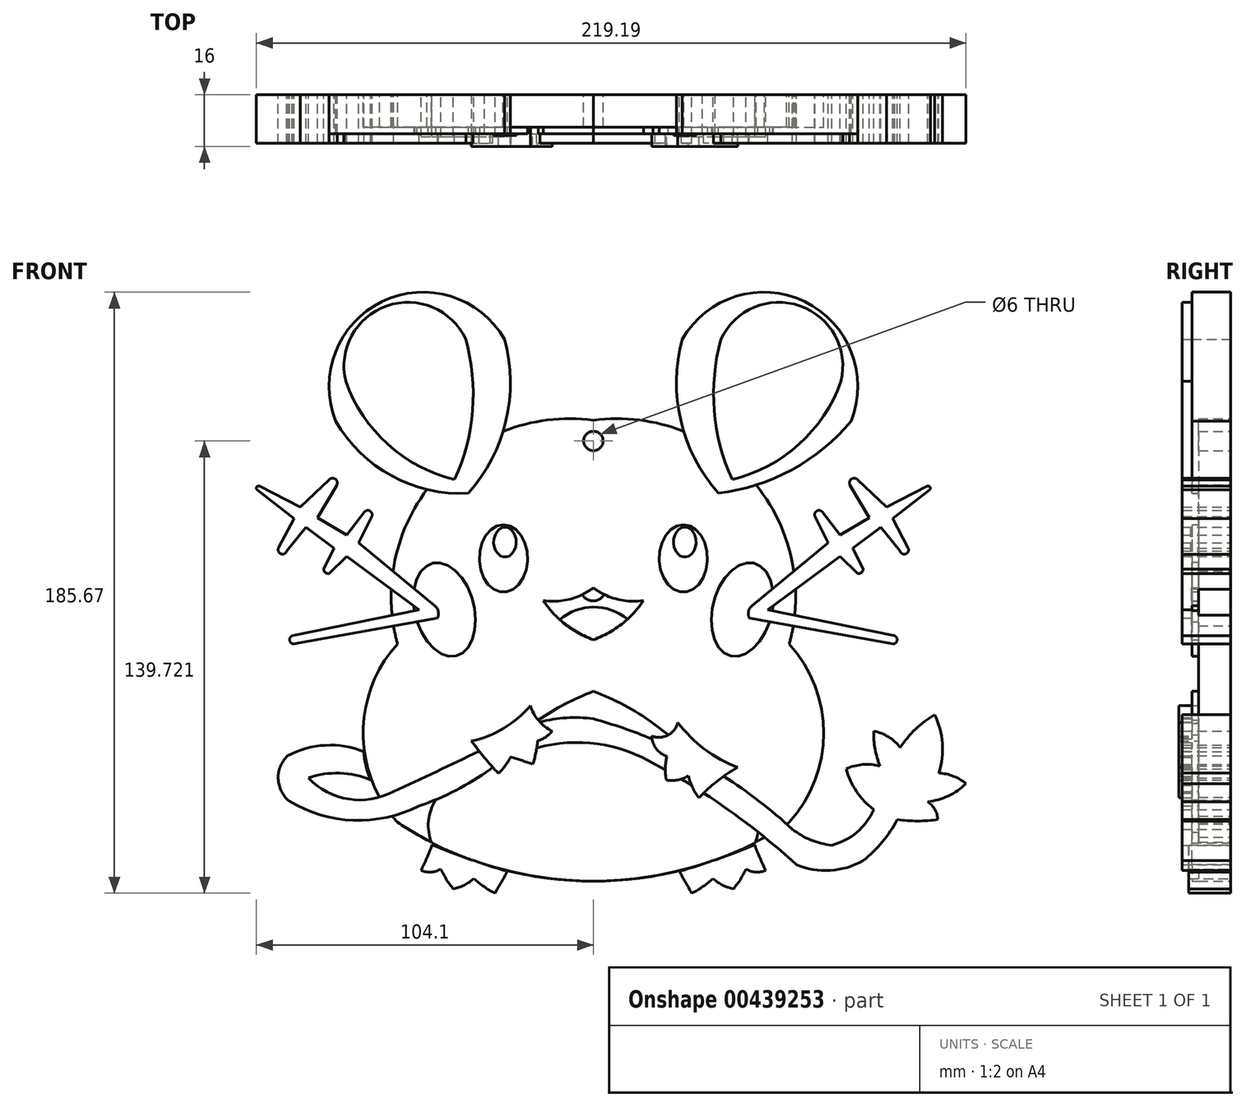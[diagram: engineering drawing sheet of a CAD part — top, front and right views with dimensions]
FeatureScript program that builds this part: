
annotation { "Feature Type Name" : "Feature", "Feature Type Description" : "" }
export const myFeature = defineFeature(function(context is Context, id is Id, definition is map)
    precondition{}
    {
        {
            var Q0;
            Q0=qCreatedBy(makeId("Front.planeOp"),FACE);
            var sketch = newSketch(context, id + "F0", { "sketchPlane" : qUnion([Q0])});
            skPoint(sketch, "E0", {"position": v(-60.51, 0) * mm});
            skPoint(sketch, "E1", {"position": v(0, 69.06) * mm});
            skArc(sketch, "E2", {"start": v(0, 69.06) * mm, "mid": v(-48.84, 50.82) * mm, "end": v(-60.51, 0) * mm});
            skLineSegment(sketch, "E3", {"start": v(0, 69.06) * mm, "end": v(0, -72.21) * mm, "construction": true});
            skArc(sketch, "E4.MirrorCS", {"start": v(0, 69.06) * mm, "mid": v(48.84, 50.82) * mm, "end": v(60.51, 0) * mm});
            skPoint(sketch, "E5", {"position": v(-60.51, -55.13) * mm});
            skArc(sketch, "E6", {"start": v(-60.51, 0) * mm, "mid": v(-71.12, -27.56) * mm, "end": v(-60.51, -55.13) * mm});
            skArc(sketch, "E7.MirrorCS", {"start": v(60.51, 0) * mm, "mid": v(71.12, -27.56) * mm, "end": v(60.51, -55.13) * mm});
            skArc(sketch, "E8", {"start": v(-60.51, -55.13) * mm, "mid": v(0, -73.32) * mm, "end": v(60.51, -55.13) * mm});
            skSolve(sketch);
        }
        {
            var Q0;
            Q0=qCreatedBy(makeId("Front.planeOp"),FACE);
            var sketch = newSketch(context, id + "F1", { "sketchPlane" : qUnion([Q0])});
            skEllipse(sketch, "E9", {"center": v(-27.78, 26.42) * mm, "majorRadius": 10.45 * mm, "minorRadius": 7.45 * mm, "majorAxis": v(0, 1)});
            skEllipse(sketch, "E10", {"center": v(-46, 10.64) * mm, "majorRadius": 14.77 * mm, "minorRadius": 9.16 * mm, "majorAxis": v(-0.25, 0.97)});
            skEllipse(sketch, "E11.MirrorC", {"center": v(46, 10.64) * mm, "majorRadius": 14.77 * mm, "minorRadius": 9.16 * mm, "majorAxis": v(0.25, 0.97)});
            skEllipse(sketch, "E12.MirrorC", {"center": v(27.78, 26.42) * mm, "majorRadius": 10.45 * mm, "minorRadius": 7.45 * mm, "majorAxis": v(0, 1)});
            skEllipse(sketch, "E13", {"center": v(-27.3, 31.45) * mm, "majorRadius": 4.6 * mm, "minorRadius": 3.5 * mm, "majorAxis": v(0, 1)});
            skPoint(sketch, "E14.endSnap0", {"position": v(-30.8, 31.45) * mm});
            skPoint(sketch, "E15", {"position": v(-34.3, 31.45) * mm});
            skPoint(sketch, "E16", {"position": v(21.25, 31.45) * mm});
            skPoint(sketch, "E17", {"position": v(28.25, 31.45) * mm});
            skPoint(sketch, "E18", {"position": v(-27.3, 36.05) * mm});
            skLineSegment(sketch, "E19", {"start": v(28.25, 36.05) * mm, "end": v(28.25, 40.65) * mm});
            skPoint(sketch, "E20", {"position": v(28.25, 36.05) * mm});
            skEllipse(sketch, "E21", {"center": v(28.25, 31.45) * mm, "majorRadius": 4.6 * mm, "minorRadius": 3.5 * mm, "majorAxis": v(0, 1)});
            skPoint(sketch, "E22", {"position": v(-23.8, 31.45) * mm});
            skPoint(sketch, "E23", {"position": v(24.75, 31.45) * mm});
            skPoint(sketch, "E24", {"position": v(31.75, 31.45) * mm});
            skPoint(sketch, "E14.end.orphan", {"position": v(-36.36, 31.45) * mm});
            skPoint(sketch, "E25", {"position": v(0, 17.34) * mm});
            skPoint(sketch, "E26", {"position": v(-18.45, 14.06) * mm});
            skArc(sketch, "E27", {"start": v(-18.45, 14.06) * mm, "mid": v(-8.83, 13.48) * mm, "end": v(0, 17.34) * mm});
            skArc(sketch, "E28.MirrorCS", {"start": v(18.45, 14.06) * mm, "mid": v(8.83, 13.48) * mm, "end": v(0, 17.34) * mm});
            skPoint(sketch, "E29", {"position": v(0, 0) * mm});
            skPoint(sketch, "E30", {"position": v(0, 1.29) * mm});
            skPoint(sketch, "E31", {"position": v(0, 10.13) * mm});
            skPoint(sketch, "E32", {"position": v(-5.69, 14.3) * mm});
            skArc(sketch, "E33", {"start": v(-5.69, 14.3) * mm, "mid": v(-3.15, 11.8) * mm, "end": v(0, 10.13) * mm});
            skArc(sketch, "E34.MirrorCS", {"start": v(5.69, 14.3) * mm, "mid": v(3.15, 11.8) * mm, "end": v(0, 10.13) * mm});
            skArc(sketch, "E35", {"start": v(-15.44, 13.38) * mm, "mid": v(-8.7, 6.08) * mm, "end": v(0, 1.29) * mm});
            skArc(sketch, "E36.MirrorCS", {"start": v(15.44, 13.38) * mm, "mid": v(8.7, 6.08) * mm, "end": v(0, 1.29) * mm});
            skPoint(sketch, "E37", {"position": v(-79.58, 68.87) * mm});
            skPoint(sketch, "E38", {"position": v(-38.6, 46.57) * mm});
            skPoint(sketch, "E39", {"position": v(-27.45, 94.11) * mm});
            skArc(sketch, "E40", {"start": v(-79.58, 68.87) * mm, "mid": v(-62.27, 51.88) * mm, "end": v(-38.6, 46.57) * mm});
            skArc(sketch, "E41", {"start": v(-38.6, 46.57) * mm, "mid": v(-27, 68.93) * mm, "end": v(-27.45, 94.11) * mm});
            skArc(sketch, "E42", {"start": v(-27.45, 94.11) * mm, "mid": v(-65.26, 105.75) * mm, "end": v(-79.58, 68.87) * mm});
            skArc(sketch, "E43.MirrorCS", {"start": v(38.6, 46.57) * mm, "mid": v(27, 68.93) * mm, "end": v(27.45, 94.11) * mm});
            skArc(sketch, "E44.MirrorCS", {"start": v(27.45, 94.11) * mm, "mid": v(65.26, 105.75) * mm, "end": v(79.58, 68.87) * mm});
            skArc(sketch, "E45", {"start": v(38.6, 46.57) * mm, "mid": v(61.26, 53.74) * mm, "end": v(79.58, 68.87) * mm});
            skPoint(sketch, "E46", {"position": v(0, -14.65) * mm});
            skPoint(sketch, "E47", {"position": v(-18.44, -24.49) * mm});
            skPoint(sketch, "E48", {"position": v(-49.92, -61.53) * mm});
            skPoint(sketch, "E49", {"position": v(-48.16, -47.4) * mm});
            skArc(sketch, "E50", {"start": v(0, -14.65) * mm, "mid": v(-9.54, -18.97) * mm, "end": v(-18.44, -24.49) * mm});
            skArc(sketch, "E51", {"start": v(-48.16, -47.4) * mm, "mid": v(-50.9, -54.23) * mm, "end": v(-49.92, -61.53) * mm});
            skLineSegment(sketch, "E52", {"start": v(-18.44, -24.49) * mm, "end": v(-48.16, -47.4) * mm});
            skArc(sketch, "E53.MirrorCS", {"start": v(0, -14.65) * mm, "mid": v(9.54, -18.97) * mm, "end": v(18.44, -24.49) * mm});
            skLineSegment(sketch, "E54.MirrorCS", {"start": v(18.44, -24.49) * mm, "end": v(48.16, -47.4) * mm});
            skArc(sketch, "E55.MirrorCS", {"start": v(48.16, -47.4) * mm, "mid": v(50.9, -54.23) * mm, "end": v(49.92, -61.53) * mm});
            skArc(sketch, "E56", {"start": v(-49.92, -61.53) * mm, "mid": v(0, -73.23) * mm, "end": v(49.92, -61.53) * mm});
            skSolve(sketch);
        }
        {
            var Q0;
            Q0=qCreatedBy(makeId("Front.planeOp"),FACE);
            var sketch = newSketch(context, id + "F2", { "sketchPlane" : qUnion([Q0])});
            skLineSegment(sketch, "E57", {"start": v(-48.16, 7.98) * mm, "end": v(-92.67, 0) * mm});
            skPoint(sketch, "E58", {"position": v(-93.06, 2.5) * mm});
            skPoint(sketch, "E59", {"position": v(-48.96, 11.76) * mm});
            skArc(sketch, "E60", {"start": v(-93.06, 2.5) * mm, "mid": v(-93.82, 1.1) * mm, "end": v(-92.67, 0) * mm});
            skArc(sketch, "E61", {"start": v(-48.16, 7.98) * mm, "mid": v(-47.9, 10.01) * mm, "end": v(-48.96, 11.76) * mm});
            skLineSegment(sketch, "E62", {"start": v(-93.06, 2.5) * mm, "end": v(-53.87, 10.6) * mm});
            skLineSegment(sketch, "E63", {"start": v(-53.87, 10.6) * mm, "end": v(-76.2, 27) * mm});
            skLineSegment(sketch, "E64", {"start": v(-76.2, 27) * mm, "end": v(-81.72, 21.76) * mm});
            skLineSegment(sketch, "E65", {"start": v(-48.96, 11.76) * mm, "end": v(-72.48, 31.21) * mm});
            skLineSegment(sketch, "E66", {"start": v(-72.48, 31.21) * mm, "end": v(-68.43, 39.4) * mm});
            skPoint(sketch, "E67", {"position": v(-83.3, 23.07) * mm});
            skPoint(sketch, "E68", {"position": v(-70.75, 40.72) * mm});
            skPoint(sketch, "E69", {"position": v(-79.3, 48.99) * mm});
            skPoint(sketch, "E70", {"position": v(-81.72, 50.64) * mm});
            skPoint(sketch, "E71", {"position": v(-103.83, 47.6) * mm});
            skPoint(sketch, "E72", {"position": v(-103.15, 48.71) * mm});
            skPoint(sketch, "E73", {"position": v(-97.22, 29.69) * mm});
            skPoint(sketch, "E74", {"position": v(-94.74, 28.72) * mm});
            skLineSegment(sketch, "E75", {"start": v(-80.13, 29.55) * mm, "end": v(-87.57, 35.2) * mm});
            skLineSegment(sketch, "E76", {"start": v(-79.3, 48.99) * mm, "end": v(-85.23, 38.92) * mm});
            skLineSegment(sketch, "E77", {"start": v(-85.23, 38.92) * mm, "end": v(-76.2, 33.6) * mm});
            skLineSegment(sketch, "E78", {"start": v(-76.2, 33.6) * mm, "end": v(-70.75, 40.72) * mm});
            skLineSegment(sketch, "E79", {"start": v(-97.22, 29.69) * mm, "end": v(-92.4, 38.79) * mm});
            skLineSegment(sketch, "E80", {"start": v(-92.4, 38.79) * mm, "end": v(-103.83, 47.6) * mm});
            skLineSegment(sketch, "E81", {"start": v(-103.15, 48.71) * mm, "end": v(-90.6, 42.23) * mm});
            skLineSegment(sketch, "E82", {"start": v(-90.6, 42.23) * mm, "end": v(-81.72, 50.64) * mm});
            skArc(sketch, "E83", {"start": v(-103.15, 48.71) * mm, "mid": v(-104, 48.48) * mm, "end": v(-103.83, 47.6) * mm});
            skArc(sketch, "E84", {"start": v(-97.22, 29.69) * mm, "mid": v(-96.52, 27.81) * mm, "end": v(-94.74, 28.72) * mm});
            skLineSegment(sketch, "E85", {"start": v(-94.74, 28.72) * mm, "end": v(-88.74, 36.09) * mm});
            skLineSegment(sketch, "E86", {"start": v(-88.74, 36.09) * mm, "end": v(-87.57, 35.2) * mm});
            skArc(sketch, "E87", {"start": v(-79.3, 48.99) * mm, "mid": v(-79.73, 50.94) * mm, "end": v(-81.72, 50.64) * mm});
            skArc(sketch, "E88", {"start": v(-68.43, 39.4) * mm, "mid": v(-69.02, 41.07) * mm, "end": v(-70.75, 40.72) * mm});
            skArc(sketch, "E89", {"start": v(-83.3, 23.07) * mm, "mid": v(-82.8, 22.05) * mm, "end": v(-81.72, 21.76) * mm});
            skLineSegment(sketch, "E90", {"start": v(-80.13, 29.55) * mm, "end": v(-83.3, 23.07) * mm});
            skLineSegment(sketch, "E91.MirrorCS", {"start": v(103.15, 48.71) * mm, "end": v(90.6, 42.23) * mm});
            skArc(sketch, "E92.MirrorCS", {"start": v(103.15, 48.71) * mm, "mid": v(104, 48.48) * mm, "end": v(103.83, 47.6) * mm});
            skLineSegment(sketch, "E93.MirrorCS", {"start": v(92.4, 38.79) * mm, "end": v(103.83, 47.6) * mm});
            skLineSegment(sketch, "E94.MirrorCS", {"start": v(90.6, 42.23) * mm, "end": v(81.72, 50.64) * mm});
            skArc(sketch, "E95.MirrorCS", {"start": v(79.3, 48.99) * mm, "mid": v(79.73, 50.94) * mm, "end": v(81.72, 50.64) * mm});
            skLineSegment(sketch, "E96.MirrorCS", {"start": v(79.3, 48.99) * mm, "end": v(85.23, 38.92) * mm});
            skLineSegment(sketch, "E97.MirrorCS", {"start": v(97.22, 29.69) * mm, "end": v(92.4, 38.79) * mm});
            skArc(sketch, "E98.MirrorCS", {"start": v(97.22, 29.69) * mm, "mid": v(96.52, 27.81) * mm, "end": v(94.74, 28.72) * mm});
            skLineSegment(sketch, "E99.MirrorCS", {"start": v(94.74, 28.72) * mm, "end": v(88.74, 36.09) * mm});
            skLineSegment(sketch, "E100.MirrorCS", {"start": v(80.13, 29.55) * mm, "end": v(87.57, 35.2) * mm});
            skLineSegment(sketch, "E101.MirrorCS", {"start": v(88.74, 36.09) * mm, "end": v(87.57, 35.2) * mm});
            skLineSegment(sketch, "E102.MirrorCS", {"start": v(80.13, 29.55) * mm, "end": v(83.3, 23.07) * mm});
            skArc(sketch, "E103.MirrorCS", {"start": v(83.3, 23.07) * mm, "mid": v(82.8, 22.05) * mm, "end": v(81.72, 21.76) * mm});
            skLineSegment(sketch, "E104.MirrorCS", {"start": v(76.2, 27) * mm, "end": v(81.72, 21.76) * mm});
            skLineSegment(sketch, "E105.MirrorCS", {"start": v(53.87, 10.6) * mm, "end": v(76.2, 27) * mm});
            skLineSegment(sketch, "E106.MirrorCS", {"start": v(76.2, 33.6) * mm, "end": v(70.75, 40.72) * mm});
            skArc(sketch, "E107.MirrorCS", {"start": v(68.43, 39.4) * mm, "mid": v(69.02, 41.07) * mm, "end": v(70.75, 40.72) * mm});
            skLineSegment(sketch, "E108.MirrorCS", {"start": v(72.48, 31.21) * mm, "end": v(68.43, 39.4) * mm});
            skLineSegment(sketch, "E109.MirrorCS", {"start": v(48.96, 11.76) * mm, "end": v(72.48, 31.21) * mm});
            skArc(sketch, "E110.MirrorCS", {"start": v(48.16, 7.98) * mm, "mid": v(47.9, 10.01) * mm, "end": v(48.96, 11.76) * mm});
            skLineSegment(sketch, "E111.MirrorCS", {"start": v(48.16, 7.98) * mm, "end": v(92.67, 0) * mm});
            skLineSegment(sketch, "E112.MirrorCS", {"start": v(93.06, 2.5) * mm, "end": v(53.87, 10.6) * mm});
            skArc(sketch, "E113.MirrorCS", {"start": v(93.06, 2.5) * mm, "mid": v(93.82, 1.1) * mm, "end": v(92.67, 0) * mm});
            skPoint(sketch, "E114", {"position": v(-70.89, -33.3) * mm});
            skPoint(sketch, "E115", {"position": v(-94.5, -34.6) * mm});
            skPoint(sketch, "E116", {"position": v(-94, -48.54) * mm});
            skPoint(sketch, "E117", {"position": v(-53.84, -50.01) * mm});
            skPoint(sketch, "E118", {"position": v(-31.87, -38.7) * mm});
            skPoint(sketch, "E119", {"position": v(19.1, -37.23) * mm});
            skPoint(sketch, "E120", {"position": v(62.71, -68.21) * mm});
            skPoint(sketch, "E121", {"position": v(83.37, -66.9) * mm});
            skPoint(sketch, "E122", {"position": v(93.86, -54.29) * mm});
            skPoint(sketch, "E123", {"position": v(106.4, -54.29) * mm});
            skPoint(sketch, "E124", {"position": v(103.29, -48.74) * mm});
            skPoint(sketch, "E125", {"position": v(115.1, -43.17) * mm});
            skPoint(sketch, "E126", {"position": v(106.73, -39.89) * mm});
            skPoint(sketch, "E127", {"position": v(105.42, -21.85) * mm});
            skPoint(sketch, "E128", {"position": v(94.76, -32.02) * mm});
            skPoint(sketch, "E129", {"position": v(86.57, -26.94) * mm});
            skPoint(sketch, "E130", {"position": v(88.54, -37.76) * mm});
            skPoint(sketch, "E131", {"position": v(78.04, -38.58) * mm});
            skPoint(sketch, "E132", {"position": v(86.57, -51.2) * mm});
            skPoint(sketch, "E133", {"position": v(73.62, -62.18) * mm});
            skPoint(sketch, "E134", {"position": v(61.49, -57.26) * mm});
            skPoint(sketch, "E135", {"position": v(0, -23.17) * mm});
            skPoint(sketch, "E136", {"position": v(-18.84, -24.8) * mm});
            skArc(sketch, "E137", {"start": v(94.76, -32.02) * mm, "mid": v(91.14, -28.71) * mm, "end": v(86.57, -26.94) * mm});
            skArc(sketch, "E138", {"start": v(105.42, -21.85) * mm, "mid": v(99.52, -26.34) * mm, "end": v(94.76, -32.02) * mm});
            skArc(sketch, "E139", {"start": v(106.73, -39.89) * mm, "mid": v(107.82, -30.74) * mm, "end": v(105.42, -21.85) * mm});
            skArc(sketch, "E140", {"start": v(115.1, -43.17) * mm, "mid": v(111.17, -40.86) * mm, "end": v(106.73, -39.89) * mm});
            skArc(sketch, "E141", {"start": v(103.29, -48.74) * mm, "mid": v(109.66, -46.95) * mm, "end": v(115.1, -43.17) * mm});
            skArc(sketch, "E142", {"start": v(106.4, -54.29) * mm, "mid": v(105.49, -51.15) * mm, "end": v(103.29, -48.74) * mm});
            skArc(sketch, "E143", {"start": v(93.86, -54.29) * mm, "mid": v(100.13, -54.7) * mm, "end": v(106.4, -54.29) * mm});
            skArc(sketch, "E144", {"start": v(78.04, -38.58) * mm, "mid": v(81.27, -45.59) * mm, "end": v(86.57, -51.2) * mm});
            skArc(sketch, "E145", {"start": v(88.54, -37.76) * mm, "mid": v(83.22, -37.27) * mm, "end": v(78.04, -38.58) * mm});
            skArc(sketch, "E146", {"start": v(86.57, -26.94) * mm, "mid": v(87.01, -32.44) * mm, "end": v(88.54, -37.76) * mm});
            skArc(sketch, "E147", {"start": v(73.62, -62.18) * mm, "mid": v(81.39, -58.21) * mm, "end": v(86.57, -51.2) * mm});
            skArc(sketch, "E148", {"start": v(61.49, -57.26) * mm, "mid": v(67.2, -60.57) * mm, "end": v(73.62, -62.18) * mm});
            skArc(sketch, "E149", {"start": v(61.49, -57.26) * mm, "mid": v(32.8, -36.5) * mm, "end": v(0, -23.17) * mm});
            skArc(sketch, "E150", {"start": v(0, -23.17) * mm, "mid": v(-9.51, -22.93) * mm, "end": v(-18.84, -24.8) * mm});
            skArc(sketch, "E151", {"start": v(83.37, -66.9) * mm, "mid": v(89.26, -61.14) * mm, "end": v(93.86, -54.29) * mm});
            skArc(sketch, "E152", {"start": v(62.71, -68.21) * mm, "mid": v(73.2, -69.99) * mm, "end": v(83.37, -66.9) * mm});
            skArc(sketch, "E153", {"start": v(62.71, -68.21) * mm, "mid": v(41.87, -51.37) * mm, "end": v(19.1, -37.23) * mm});
            skArc(sketch, "E154", {"start": v(19.1, -37.23) * mm, "mid": v(-6.6, -30.48) * mm, "end": v(-31.87, -38.7) * mm});
            skArc(sketch, "E155", {"start": v(-53.84, -50.01) * mm, "mid": v(-42.41, -45.22) * mm, "end": v(-31.87, -38.7) * mm});
            skArc(sketch, "E156", {"start": v(-94, -48.54) * mm, "mid": v(-74.11, -54.48) * mm, "end": v(-53.84, -50.01) * mm});
            skArc(sketch, "E157", {"start": v(-94.5, -34.6) * mm, "mid": v(-97.37, -41.68) * mm, "end": v(-94, -48.54) * mm});
            skArc(sketch, "E158", {"start": v(-70.89, -33.3) * mm, "mid": v(-82.84, -31.32) * mm, "end": v(-94.5, -34.6) * mm});
            skArc(sketch, "E159", {"start": v(-70.89, -33.3) * mm, "mid": v(-70.25, -37.76) * mm, "end": v(-68.8, -42.03) * mm});
            skArc(sketch, "E160", {"start": v(-68.8, -42.03) * mm, "mid": v(-78.34, -39.94) * mm, "end": v(-88.02, -41.35) * mm});
            skArc(sketch, "E161", {"start": v(-88.02, -41.35) * mm, "mid": v(-75.61, -47.94) * mm, "end": v(-61.77, -45.54) * mm});
            skArc(sketch, "E162", {"start": v(-61.77, -45.54) * mm, "mid": v(-40.15, -35.48) * mm, "end": v(-18.84, -24.8) * mm});
            skPoint(sketch, "E163", {"position": v(-49.8, -62.04) * mm});
            skPoint(sketch, "E164", {"position": v(-52.75, -69.75) * mm});
            skPoint(sketch, "E165", {"position": v(-47.17, -69.9) * mm});
            skPoint(sketch, "E166", {"position": v(-43.4, -75.48) * mm});
            skPoint(sketch, "E167", {"position": v(-36.52, -72.53) * mm});
            skPoint(sketch, "E168", {"position": v(-30.45, -77.29) * mm});
            skPoint(sketch, "E169", {"position": v(-26.85, -70.24) * mm});
            skArc(sketch, "E170", {"start": v(-49.8, -62.04) * mm, "mid": v(-51.37, -65.86) * mm, "end": v(-52.75, -69.75) * mm});
            skArc(sketch, "E171", {"start": v(-52.75, -69.75) * mm, "mid": v(-49.97, -70.3) * mm, "end": v(-47.17, -69.9) * mm});
            skArc(sketch, "E172", {"start": v(-47.17, -69.9) * mm, "mid": v(-45.46, -72.81) * mm, "end": v(-43.4, -75.48) * mm});
            skArc(sketch, "E173", {"start": v(-43.4, -75.48) * mm, "mid": v(-39.78, -74.42) * mm, "end": v(-36.52, -72.53) * mm});
            skArc(sketch, "E174", {"start": v(-36.52, -72.53) * mm, "mid": v(-33.57, -75.02) * mm, "end": v(-30.45, -77.29) * mm});
            skArc(sketch, "E175", {"start": v(-30.45, -77.29) * mm, "mid": v(-28.52, -73.83) * mm, "end": v(-26.85, -70.24) * mm});
            skArc(sketch, "E176.MirrorCS", {"start": v(49.8, -62.04) * mm, "mid": v(51.37, -65.86) * mm, "end": v(52.75, -69.75) * mm});
            skArc(sketch, "E177.MirrorCS", {"start": v(52.75, -69.75) * mm, "mid": v(49.97, -70.3) * mm, "end": v(47.17, -69.9) * mm});
            skArc(sketch, "E178.MirrorCS", {"start": v(47.17, -69.9) * mm, "mid": v(45.46, -72.81) * mm, "end": v(43.4, -75.48) * mm});
            skArc(sketch, "E179.MirrorCS", {"start": v(43.4, -75.48) * mm, "mid": v(39.78, -74.42) * mm, "end": v(36.52, -72.53) * mm});
            skArc(sketch, "E180.MirrorCS", {"start": v(36.52, -72.53) * mm, "mid": v(33.57, -75.02) * mm, "end": v(30.45, -77.29) * mm});
            skArc(sketch, "E181.MirrorCS", {"start": v(30.45, -77.29) * mm, "mid": v(28.52, -73.83) * mm, "end": v(26.85, -70.24) * mm});
            skPoint(sketch, "E182", {"position": v(-42.87, 50.73) * mm});
            skPoint(sketch, "E183", {"position": v(-39.4, 94.09) * mm});
            skPoint(sketch, "E184", {"position": v(-76.49, 81.1) * mm});
            skArc(sketch, "E185", {"start": v(-42.87, 50.73) * mm, "mid": v(-37.35, 72.1) * mm, "end": v(-39.4, 94.09) * mm});
            skArc(sketch, "E186", {"start": v(-76.49, 81.1) * mm, "mid": v(-63.51, 61.68) * mm, "end": v(-42.87, 50.73) * mm});
            skArc(sketch, "E187", {"start": v(-39.4, 94.09) * mm, "mid": v(-63.83, 104.42) * mm, "end": v(-76.49, 81.1) * mm});
            skArc(sketch, "E188.MirrorCS", {"start": v(76.49, 81.1) * mm, "mid": v(63.51, 61.68) * mm, "end": v(42.87, 50.73) * mm});
            skArc(sketch, "E189.MirrorCS", {"start": v(39.4, 94.09) * mm, "mid": v(63.83, 104.42) * mm, "end": v(76.49, 81.1) * mm});
            skArc(sketch, "E190.MirrorCS", {"start": v(42.87, 50.73) * mm, "mid": v(37.35, 72.1) * mm, "end": v(39.4, 94.09) * mm});
            skArc(sketch, "E191", {"start": v(-49.73, -62) * mm, "mid": v(-38.7, -67.26) * mm, "end": v(-26.85, -70.24) * mm});
            skArc(sketch, "E192.MirrorCS", {"start": v(49.73, -62) * mm, "mid": v(38.7, -67.26) * mm, "end": v(26.85, -70.24) * mm});
            skLineSegment(sketch, "E193", {"start": v(76.2, 33.6) * mm, "end": v(85.23, 38.92) * mm});
            skSolve(sketch);
        }
        {
            var Q0;
            Q0=qCreatedBy(makeId("Front.planeOp"),FACE);
            var sketch = newSketch(context, id + "F3", { "sketchPlane" : qUnion([Q0])});
            skCircle(sketch, "E194", {"center": v(0, 62.7) * mm, "radius": 4 * mm});
            skSolve(sketch);
        }
        {
            var Q0;
            Q0 = qSketchRegion(id + "F0", true);
            extrude(context, id + "F4", {"entities" : qUnion([Q0]), "depth" : 10 * mm, "offsetDistance" : 25 * mm});
        }
        {
            var Q0;
            Q0 = qSketchRegion(id + "F1", true);
            extrude(context, id + "F5", {"entities" : qUnion([Q0]), "operationType" : NewBodyOperationType.ADD, "depth" : 12 * mm, "offsetDistance" : 25 * mm});
        }
        {
            var Q0;
            Q0=makeQuery(id+"F5.opExtrude","CAP_FACE",FACE,{"disambiguationData":[OSD([sQuery(id+"F1.wireOp",EDGE,"E27"),sQuery(id+"F1.wireOp",EDGE,"E28.MirrorCS"),sQuery(id+"F1.wireOp",EDGE,"E35"),sQuery(id+"F1.wireOp",EDGE,"E36.MirrorCS")])],"isStart":false});
            var sketch = newSketch(context, id + "F6", { "sketchPlane" : qUnion([Q0])});
            skArc(sketch, "E195", {"start": v(10.55, 7.64) * mm, "mid": v(0.05, 11.38) * mm, "end": v(-10.39, 7.49) * mm});
            skArc(sketch, "E196", {"start": v(-10.39, 7.49) * mm, "mid": v(-5.46, 3.94) * mm, "end": v(0, 1.29) * mm});
            skArc(sketch, "E197", {"start": v(0, 1.29) * mm, "mid": v(5.59, 3.94) * mm, "end": v(10.55, 7.64) * mm});
            skSolve(sketch);
        }
        {
            var Q0;
            Q0=makeQuery(id+"F6.imprint","IMPRINT",FACE,{"disambiguationData":[TD([[makeQuery(id+"F6.imprint","IMPRINT",EDGE,{"derivedFrom":sQuery(id+"F6.wireOp",EDGE,"E195")}),1.0]])]});
            extrude(context, id + "F7", {"entities" : qUnion([Q0]), "operationType" : NewBodyOperationType.ADD, "depth" : 0.1 * mm, "offsetDistance" : 25 * mm});
        }
        {
            var Q0;
            Q0=makeQuery(id+"F5.boolean.opBoolean","SPLIT",FACE,{"disambiguationData":[TD([makeQuery(id+"F5.opExtrude","SWEPT_FACE",FACE,{"disambiguationData":[OSD([sQuery(id+"F1.wireOp",EDGE,"E13")])]})])],"derivedFrom":makeQuery(id+"F4.opExtrude","CAP_FACE",FACE,{"disambiguationData":[OSD([sQuery(id+"F0.wireOp",EDGE,"E2"),sQuery(id+"F0.wireOp",EDGE,"E4.MirrorCS"),sQuery(id+"F0.wireOp",EDGE,"E6"),sQuery(id+"F0.wireOp",EDGE,"E7.MirrorCS"),sQuery(id+"F0.wireOp",EDGE,"E8")])],"isStart":false})});
            var Q1;
            Q1=makeQuery(id+"F5.boolean.opBoolean","SPLIT",FACE,{"disambiguationData":[TD([makeQuery(id+"F5.opExtrude","SWEPT_FACE",FACE,{"disambiguationData":[OSD([sQuery(id+"F1.wireOp",EDGE,"E21")])]})])],"derivedFrom":makeQuery(id+"F4.opExtrude","CAP_FACE",FACE,{"disambiguationData":[OSD([sQuery(id+"F0.wireOp",EDGE,"E2"),sQuery(id+"F0.wireOp",EDGE,"E4.MirrorCS"),sQuery(id+"F0.wireOp",EDGE,"E6"),sQuery(id+"F0.wireOp",EDGE,"E7.MirrorCS"),sQuery(id+"F0.wireOp",EDGE,"E8")])],"isStart":false})});
            extrude(context, id + "F8", {"entities" : qUnion([Q0, Q1]), "operationType" : NewBodyOperationType.ADD, "depth" : 2.5 * mm, "offsetDistance" : 25 * mm});
        }
        {
            var Q0;
            {var subQ0=sQuery(id+"F1.wireOp",EDGE,"E35");var subQ1=sQuery(id+"F1.wireOp",EDGE,"E28.MirrorCS");var subQ2=sQuery(id+"F1.wireOp",EDGE,"E36.MirrorCS");var subQ3=sQuery(id+"F1.wireOp",EDGE,"E27");var subQ4=makeQuery(id+"F5.opExtrude","CAP_FACE",FACE,{"disambiguationData":[OSD([subQ3,subQ1,subQ0,subQ2])],"isStart":false});Q0=makeQuery(id+"F7.boolean.opBoolean","SPLIT",FACE,{"disambiguationData":[TD([makeQuery(id+"F5.opExtrude","SWEPT_FACE",FACE,{"disambiguationData":[OSD([subQ3])]}),subQ4,makeQuery(id+"F5.opExtrude","SWEPT_FACE",FACE,{"disambiguationData":[OSD([subQ1])]}),makeQuery(id+"F5.opExtrude","SWEPT_FACE",FACE,{"disambiguationData":[OSD([subQ0])]}),makeQuery(id+"F5.opExtrude","SWEPT_FACE",FACE,{"disambiguationData":[OSD([subQ2])]}),makeQuery(id+"F7.opExtrude","SWEPT_FACE",FACE,{"disambiguationData":[OSD([sQuery(id+"F6.wireOp",EDGE,"E195")])]}),makeQuery(id+"F7.opExtrude","SWEPT_FACE",FACE,{"disambiguationData":[OSD([sQuery(id+"F6.wireOp",EDGE,"E196")])]}),makeQuery(id+"F7.opExtrude","SWEPT_FACE",FACE,{"disambiguationData":[OSD([sQuery(id+"F6.wireOp",EDGE,"E197")])]})])],"derivedFrom":subQ4});}
            var sketch = newSketch(context, id + "F9", { "sketchPlane" : qUnion([Q0])});
            skArc(sketch, "E198", {"start": v(-3.43, 15.23) * mm, "mid": v(-0.05, 13.27) * mm, "end": v(3.3, 15.3) * mm});
            skSolve(sketch);
        }
        {
            var Q0;
            {var subQ0=sQuery(id+"F9.wireOp",EDGE,"E198");Q0=makeQuery(id+"F9.imprint","IMPRINT",FACE,{"disambiguationData":[TD([[makeQuery(id+"F9.imprint","IMPRINT",EDGE,{"derivedFrom":subQ0}),1.0]])]});}
            extrude(context, id + "F10", {"entities" : qUnion([Q0]), "operationType" : NewBodyOperationType.ADD, "depth" : 0.1 * mm, "offsetDistance" : 25 * mm});
        }
        {
            var Q0;
            Q0 = qSketchRegion(id + "F2", true);
            extrude(context, id + "F11", {"entities" : qUnion([Q0]), "operationType" : NewBodyOperationType.ADD, "depth" : 15 * mm, "offsetDistance" : 25 * mm});
        }
        {
            var Q0;
            Q0=qCreatedBy(makeId("Front.planeOp"),FACE);
            var sketch = newSketch(context, id + "F12", { "sketchPlane" : qUnion([Q0])});
            skPoint(sketch, "E199", {"position": v(-37.67, -29.99) * mm});
            skPoint(sketch, "E200", {"position": v(-29.34, -40.02) * mm});
            skPoint(sketch, "E201", {"position": v(-25.55, -34.9) * mm});
            skPoint(sketch, "E202", {"position": v(-18.73, -37.18) * mm});
            skPoint(sketch, "E203", {"position": v(-17.22, -29.99) * mm});
            skPoint(sketch, "E204", {"position": v(-12.68, -26.96) * mm});
            skPoint(sketch, "E205", {"position": v(-19.5, -19) * mm});
            skArc(sketch, "E206", {"start": v(-37.67, -29.99) * mm, "mid": v(-33.66, -35.13) * mm, "end": v(-29.34, -40.02) * mm});
            skArc(sketch, "E207", {"start": v(-29.34, -40.02) * mm, "mid": v(-27.24, -37.61) * mm, "end": v(-25.55, -34.9) * mm});
            skArc(sketch, "E208", {"start": v(-18.73, -37.18) * mm, "mid": v(-22.12, -35.99) * mm, "end": v(-25.55, -34.9) * mm});
            skArc(sketch, "E209", {"start": v(-18.73, -37.18) * mm, "mid": v(-17.77, -33.63) * mm, "end": v(-17.22, -29.99) * mm});
            skArc(sketch, "E210", {"start": v(-17.22, -29.99) * mm, "mid": v(-14.74, -28.78) * mm, "end": v(-12.68, -26.96) * mm});
            skArc(sketch, "E211", {"start": v(-19.5, -19) * mm, "mid": v(-16.91, -23.7) * mm, "end": v(-12.68, -26.96) * mm});
            skArc(sketch, "E212", {"start": v(-37.67, -29.99) * mm, "mid": v(-27.64, -26.05) * mm, "end": v(-19.5, -19) * mm});
            skPoint(sketch, "E213", {"position": v(18.06, -28.5) * mm});
            skPoint(sketch, "E214", {"position": v(26.1, -24.22) * mm});
            skPoint(sketch, "E215", {"position": v(22.77, -34.69) * mm});
            skPoint(sketch, "E216", {"position": v(22.58, -42.07) * mm});
            skPoint(sketch, "E217", {"position": v(29.4, -40.75) * mm});
            skPoint(sketch, "E218", {"position": v(32.61, -47.56) * mm});
            skPoint(sketch, "E219", {"position": v(44.54, -38.1) * mm});
            skArc(sketch, "E220", {"start": v(18.06, -28.5) * mm, "mid": v(23.04, -28.16) * mm, "end": v(26.1, -24.22) * mm});
            skArc(sketch, "E221", {"start": v(18.06, -28.5) * mm, "mid": v(19.4, -32.37) * mm, "end": v(22.77, -34.69) * mm});
            skArc(sketch, "E222", {"start": v(22.77, -34.69) * mm, "mid": v(22.2, -38.37) * mm, "end": v(22.58, -42.07) * mm});
            skArc(sketch, "E223", {"start": v(22.58, -42.07) * mm, "mid": v(26.1, -42.02) * mm, "end": v(29.4, -40.75) * mm});
            skArc(sketch, "E224", {"start": v(29.4, -40.75) * mm, "mid": v(30.62, -44.33) * mm, "end": v(32.61, -47.56) * mm});
            skArc(sketch, "E225", {"start": v(44.54, -38.1) * mm, "mid": v(38.24, -42.4) * mm, "end": v(32.61, -47.56) * mm});
            skArc(sketch, "E226", {"start": v(26.1, -24.22) * mm, "mid": v(34.32, -32.49) * mm, "end": v(44.54, -38.1) * mm});
            skSolve(sketch);
        }
        {
            var Q0;
            Q0 = qSketchRegion(id + "F12", true);
            extrude(context, id + "F13", {"entities" : qUnion([Q0]), "operationType" : NewBodyOperationType.ADD, "depth" : 16 * mm, "offsetDistance" : 25 * mm});
        }
        {
            var Q0;
            Q0=qCreatedBy(makeId("Front.planeOp"),FACE);
            var sketch = newSketch(context, id + "F14", { "sketchPlane" : qUnion([Q0])});
            skPoint(sketch, "E227", {"position": v(-49.85, -62.09) * mm});
            skPoint(sketch, "E228", {"position": v(-53.24, -70) * mm});
            skPoint(sketch, "E229", {"position": v(-26.56, -70.23) * mm});
            skPoint(sketch, "E230", {"position": v(-30.4, -77.02) * mm});
            skPoint(sketch, "E231", {"position": v(-36.96, -72.5) * mm});
            skPoint(sketch, "E232", {"position": v(-43.3, -75.66) * mm});
            skPoint(sketch, "E233", {"position": v(-47.14, -69.55) * mm});
            skArc(sketch, "E234", {"start": v(-53.24, -70) * mm, "mid": v(-51.43, -66.1) * mm, "end": v(-49.85, -62.09) * mm});
            skArc(sketch, "E235", {"start": v(-53.24, -70) * mm, "mid": v(-50.14, -70.5) * mm, "end": v(-47.14, -69.55) * mm});
            skArc(sketch, "E236", {"start": v(-47.14, -69.55) * mm, "mid": v(-45.4, -72.73) * mm, "end": v(-43.3, -75.66) * mm});
            skArc(sketch, "E237", {"start": v(-43.3, -75.66) * mm, "mid": v(-39.9, -74.52) * mm, "end": v(-36.96, -72.5) * mm});
            skArc(sketch, "E238", {"start": v(-36.96, -72.5) * mm, "mid": v(-33.82, -74.96) * mm, "end": v(-30.4, -77.02) * mm});
            skArc(sketch, "E239", {"start": v(-30.4, -77.02) * mm, "mid": v(-28.44, -73.64) * mm, "end": v(-26.56, -70.23) * mm});
            skArc(sketch, "E240", {"start": v(-49.85, -62.09) * mm, "mid": v(-38.32, -66.5) * mm, "end": v(-26.56, -70.23) * mm});
            skLineSegment(sketch, "E241", {"start": v(0, -50.56) * mm, "end": v(0, -83.35) * mm, "construction": true});
            skArc(sketch, "E242.MirrorCS", {"start": v(30.4, -77.02) * mm, "mid": v(28.44, -73.64) * mm, "end": v(26.56, -70.23) * mm});
            skArc(sketch, "E243.MirrorCS", {"start": v(36.96, -72.5) * mm, "mid": v(33.82, -74.96) * mm, "end": v(30.4, -77.02) * mm});
            skArc(sketch, "E244.MirrorCS", {"start": v(43.3, -75.66) * mm, "mid": v(39.9, -74.52) * mm, "end": v(36.96, -72.5) * mm});
            skArc(sketch, "E245.MirrorCS", {"start": v(47.14, -69.55) * mm, "mid": v(45.4, -72.73) * mm, "end": v(43.3, -75.66) * mm});
            skArc(sketch, "E246.MirrorCS", {"start": v(53.24, -70) * mm, "mid": v(50.14, -70.5) * mm, "end": v(47.14, -69.55) * mm});
            skArc(sketch, "E247.MirrorCS", {"start": v(53.24, -70) * mm, "mid": v(51.43, -66.1) * mm, "end": v(49.85, -62.09) * mm});
            skArc(sketch, "E248.MirrorCS", {"start": v(49.85, -62.09) * mm, "mid": v(38.32, -66.5) * mm, "end": v(26.56, -70.23) * mm});
            skSolve(sketch);
        }
        {
            var Q0;
            Q0 = qSketchRegion(id + "F14", true);
            extrude(context, id + "F15", {"entities" : qUnion([Q0]), "operationType" : NewBodyOperationType.ADD, "depth" : 13 * mm, "offsetDistance" : 25 * mm});
        }
        {
            var Q0;
            Q0=sQuery(id+"F3.wireOp",VERTEX,"E194.center");
            var Q1;
            Q1=makeQuery(id+"F4.opExtrude","SWEPT_BODY",BODY,{"disambiguationData":[OSD([sQuery(id+"F0.wireOp",EDGE,"E2"),sQuery(id+"F0.wireOp",EDGE,"E4.MirrorCS"),sQuery(id+"F0.wireOp",EDGE,"E6"),sQuery(id+"F0.wireOp",EDGE,"E7.MirrorCS"),sQuery(id+"F0.wireOp",EDGE,"E8")])]});
            hole(context, id + "F16", {"style" : HoleStyle.C_BORE, "endStyle" : HoleEndStyle.THROUGH, "oppositeDirection" : true, "holeDiameter" : 6 * mm, "cBoreDiameter" : 6 * mm, "cBoreDepth" : 5 * mm, "isTappedThrough" : true, "tappedDepth" : 12 * mm, "tapClearance" : 3, "startFromSketch" : true, "locations" : qUnion([Q0]), "scope" : qUnion([Q1])});
        }
    });
